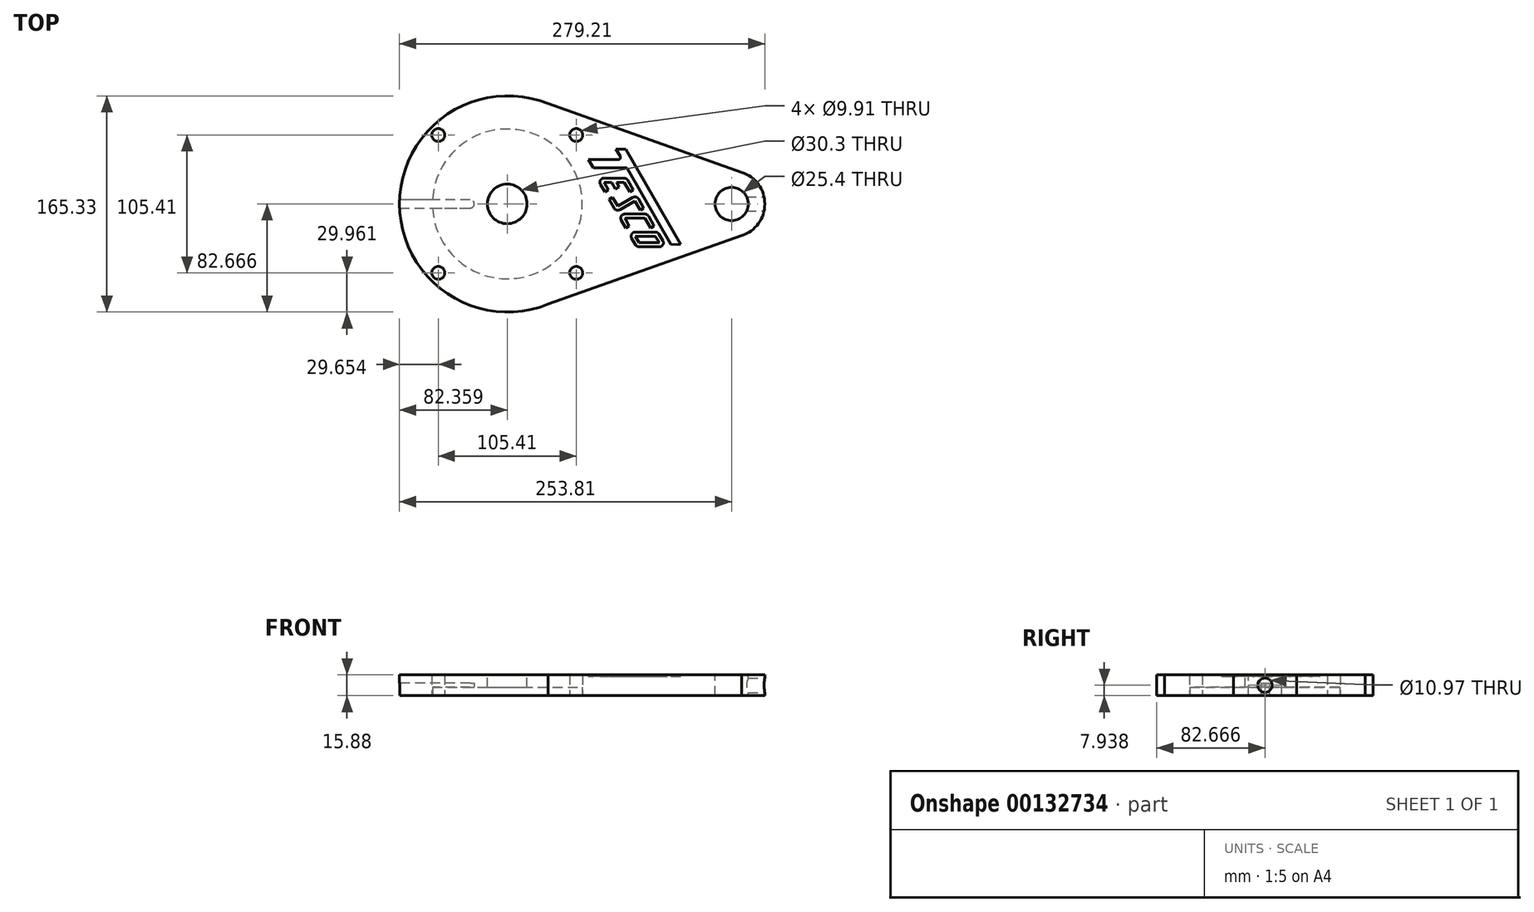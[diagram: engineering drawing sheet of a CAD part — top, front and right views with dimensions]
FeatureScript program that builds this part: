
annotation { "Feature Type Name" : "Feature", "Feature Type Description" : "" }
export const myFeature = defineFeature(function(context is Context, id is Id, definition is map)
    precondition{}
    {
        {
            var Q0;
            Q0=qCreatedBy(makeId("Top.planeOp"),FACE);
            var sketch = newSketch(context, id + "F0", { "sketchPlane" : qUnion([Q0])});
            skPoint(sketch, "E0", {"position": v(82.66, -82.66) * mm});
            skArc(sketch, "E1", {"start": v(113.6, -6) * mm, "mid": v(0, -82.66) * mm, "end": v(113.6, -159.32) * mm});
            skPoint(sketch, "E2", {"position": v(253.8, -82.66) * mm});
            skArc(sketch, "E3", {"start": v(261.56, -106.85) * mm, "mid": v(279.2, -82.66) * mm, "end": v(261.56, -58.48) * mm});
            skLineSegment(sketch, "E4", {"start": v(263.02, -59) * mm, "end": v(113.6, -6) * mm});
            skLineSegment(sketch, "E5.MirrorCS", {"start": v(263.02, -106.33) * mm, "end": v(113.6, -159.32) * mm});
            skPoint(sketch, "E6.orphan", {"position": v(279.2, -165.33) * mm});
            skPoint(sketch, "E7.orphan", {"position": v(279.2, 0) * mm});
            skPoint(sketch, "E8.orphan", {"position": v(0, 0) * mm});
            skPoint(sketch, "E9.top.start.orphan", {"position": v(0, -165.33) * mm});
            skPoint(sketch, "E10.start.orphan", {"position": v(0, -82.66) * mm});
            skPoint(sketch, "E11.trimOffspring.end.orphan", {"position": v(279.2, -82.66) * mm});
            skSolve(sketch);
        }
        {
            var Q0;
            Q0 = qSketchRegion(id + "F0", true);
            extrude(context, id + "F1", {"entities" : qUnion([Q0]), "depth" : 15.88 * mm});
        }
        {
            var Q0;
            Q0=makeQuery(id+"F1.opExtrude","CAP_FACE",FACE,{"disambiguationData":[OSD([sQuery(id+"F0.wireOp",EDGE,"E1"),sQuery(id+"F0.wireOp",EDGE,"E3"),sQuery(id+"F0.wireOp",EDGE,"E4"),sQuery(id+"F0.wireOp",EDGE,"E5.MirrorCS")])],"isStart":false});
            var sketch = newSketch(context, id + "F2", { "sketchPlane" : qUnion([Q0])});
            skLineSegment(sketch, "E12", {"start": v(0, -82.66) * mm, "end": v(279.2, -82.66) * mm});
            skPoint(sketch, "E13", {"position": v(253.8, -82.66) * mm});
            skCircle(sketch, "E14", {"center": v(253.8, -82.66) * mm, "radius": 12.7 * mm});
            skSolve(sketch);
        }
        {
            var Q0;
            Q0 = qSketchRegion(id + "F2", true);
            extrude(context, id + "F3", {"entities" : qUnion([Q0]), "operationType" : NewBodyOperationType.REMOVE, "endBound" : BoundingType.THROUGH_ALL, "oppositeDirection" : true, "depth" : 25.4 * mm});
        }
        {
            var Q0;
            Q0=makeQuery(id+"F1.opExtrude","CAP_FACE",FACE,{"disambiguationData":[OSD([sQuery(id+"F0.wireOp",EDGE,"E1"),sQuery(id+"F0.wireOp",EDGE,"E3"),sQuery(id+"F0.wireOp",EDGE,"E4"),sQuery(id+"F0.wireOp",EDGE,"E5.MirrorCS")])],"isStart":false});
            var sketch = newSketch(context, id + "F4", { "sketchPlane" : qUnion([Q0])});
            skPoint(sketch, "E15", {"position": v(82.36, -82.66) * mm});
            skPoint(sketch, "E15.positionSnap0", {"position": v(0, -82.66) * mm});
            skPoint(sketch, "E16", {"position": v(253.8, -82.66) * mm});
            skCircle(sketch, "E17", {"center": v(82.36, -82.66) * mm, "radius": 15.15 * mm});
            skSolve(sketch);
        }
        {
            var Q0;
            Q0 = qSketchRegion(id + "F4", true);
            extrude(context, id + "F5", {"entities" : qUnion([Q0]), "operationType" : NewBodyOperationType.REMOVE, "endBound" : BoundingType.THROUGH_ALL, "oppositeDirection" : true, "depth" : 25.4 * mm});
        }
        {
            var Q0;
            Q0=makeQuery(id+"F1.opExtrude","CAP_FACE",FACE,{"disambiguationData":[OSD([sQuery(id+"F0.wireOp",EDGE,"E1"),sQuery(id+"F0.wireOp",EDGE,"E3"),sQuery(id+"F0.wireOp",EDGE,"E4"),sQuery(id+"F0.wireOp",EDGE,"E5.MirrorCS")])],"isStart":true});
            var sketch = newSketch(context, id + "F6", { "sketchPlane" : qUnion([Q0])});
            skPoint(sketch, "E18", {"position": v(82.36, 82.66) * mm});
            skCircle(sketch, "E19", {"center": v(82.36, 82.66) * mm, "radius": 57.28 * mm});
            skSolve(sketch);
        }
        {
            var Q0;
            Q0 = qSketchRegion(id + "F6", true);
            extrude(context, id + "F7", {"entities" : qUnion([Q0]), "operationType" : NewBodyOperationType.REMOVE, "oppositeDirection" : true, "depth" : 6.35 * mm});
        }
        {
            var Q0;
            Q0=makeQuery(id+"F1.opExtrude","CAP_FACE",FACE,{"disambiguationData":[OSD([sQuery(id+"F0.wireOp",EDGE,"E1"),sQuery(id+"F0.wireOp",EDGE,"E3"),sQuery(id+"F0.wireOp",EDGE,"E4"),sQuery(id+"F0.wireOp",EDGE,"E5.MirrorCS")])],"isStart":true});
            var sketch = newSketch(context, id + "F8", { "sketchPlane" : qUnion([Q0])});
            skLineSegment(sketch, "E20", {"start": v(0, 82.66) * mm, "end": v(279.2, 82.66) * mm});
            skPoint(sketch, "E21", {"position": v(82.36, 82.66) * mm});
            skCircle(sketch, "E22", {"center": v(29.65, 135.37) * mm, "radius": 4.95 * mm});
            skCircle(sketch, "E23", {"center": v(135.06, 135.37) * mm, "radius": 4.95 * mm});
            skCircle(sketch, "E24", {"center": v(135.06, 29.96) * mm, "radius": 4.95 * mm});
            skCircle(sketch, "E25", {"center": v(29.65, 29.96) * mm, "radius": 4.95 * mm});
            skSolve(sketch);
        }
        {
            var Q0;
            Q0 = qSketchRegion(id + "F8", true);
            extrude(context, id + "F9", {"entities" : qUnion([Q0]), "operationType" : NewBodyOperationType.REMOVE, "endBound" : BoundingType.THROUGH_ALL, "oppositeDirection" : true, "depth" : 25.4 * mm});
        }
        {
            var Q0;
            Q0=makeQuery(id+"F1.opExtrude","CAP_FACE",FACE,{"disambiguationData":[OSD([sQuery(id+"F0.wireOp",EDGE,"E1"),sQuery(id+"F0.wireOp",EDGE,"E3"),sQuery(id+"F0.wireOp",EDGE,"E4"),sQuery(id+"F0.wireOp",EDGE,"E5.MirrorCS")])],"isStart":true});
            var sketch = newSketch(context, id + "F10", { "sketchPlane" : qUnion([Q0])});
            skPoint(sketch, "E26", {"position": v(57.15, 82.66) * mm});
            skPoint(sketch, "E27.orphan", {"position": v(82.36, 82.66) * mm});
            skLineSegment(sketch, "E28", {"start": v(53.98, 85.84) * mm, "end": v(0.06, 85.84) * mm});
            skLineSegment(sketch, "E29.MirrorCS", {"start": v(53.98, 79.49) * mm, "end": v(-1.51, 79.49) * mm});
            skLineSegment(sketch, "E30", {"start": v(57.15, 82.66) * mm, "end": v(57.15, 82.66) * mm});
            skLineSegment(sketch, "E31", {"start": v(-2.49, 85.84) * mm, "end": v(-2.49, 79.49) * mm});
            skLineSegment(sketch, "E32", {"start": v(-2.49, 79.49) * mm, "end": v(-1.51, 79.49) * mm});
            skLineSegment(sketch, "E33", {"start": v(-2.49, 85.84) * mm, "end": v(0.06, 85.84) * mm});
            skPoint(sketch, "E34.visualSharp", {"position": v(57.15, 85.84) * mm});
            skArc(sketch, "E34.filletArc", {"start": v(57.15, 82.66) * mm, "mid": v(56.22, 84.9) * mm, "end": v(53.98, 85.84) * mm});
            skPoint(sketch, "E35.visualSharp", {"position": v(57.15, 79.49) * mm});
            skArc(sketch, "E35.filletArc", {"start": v(53.98, 79.49) * mm, "mid": v(56.22, 80.42) * mm, "end": v(57.15, 82.66) * mm});
            skSolve(sketch);
        }
        {
            var Q0;
            Q0 = qSketchRegion(id + "F10", true);
            extrude(context, id + "F11", {"entities" : qUnion([Q0]), "operationType" : NewBodyOperationType.REMOVE, "oppositeDirection" : true, "depth" : 9.52 * mm});
        }
        {
            var Q0;
            Q0=qCreatedBy(makeId("Right.planeOp"),FACE);
            cPlane(context, id + "F12", {"entities" : qUnion([Q0]), "cplaneType" : CPlaneType.OFFSET, "offset" : 279.4 * mm, "width" : 152.4 * mm, "height" : 152.4 * mm});
        }
        {
            var Q0;
            Q0=qCreatedBy(id+"F12.planeOp",FACE);
            var sketch = newSketch(context, id + "F13", { "sketchPlane" : qUnion([Q0])});
            skPoint(sketch, "E36", {"position": v(-82.66, 0) * mm});
            skPoint(sketch, "E37", {"position": v(-82.66, 7.94) * mm});
            skCircle(sketch, "E38", {"center": v(-82.66, 7.94) * mm, "radius": 5.49 * mm});
            skSolve(sketch);
        }
        {
            var Q0;
            Q0 = qSketchRegion(id + "F13", true);
            extrude(context, id + "F14", {"entities" : qUnion([Q0]), "operationType" : NewBodyOperationType.REMOVE, "oppositeDirection" : true, "depth" : 15.88 * mm});
        }
        {
            var Q0;
            Q0=makeQuery(id+"F1.opExtrude","CAP_FACE",FACE,{"disambiguationData":[OSD([sQuery(id+"F0.wireOp",EDGE,"E1"),sQuery(id+"F0.wireOp",EDGE,"E3"),sQuery(id+"F0.wireOp",EDGE,"E4"),sQuery(id+"F0.wireOp",EDGE,"E5.MirrorCS")])],"isStart":false});
            var sketch = newSketch(context, id + "F15", { "sketchPlane" : qUnion([Q0])});
            skLineSegment(sketch, "E39", {"start": v(144.39, -48.66) * mm, "end": v(148.05, -55.01) * mm});
            skLineSegment(sketch, "E40", {"start": v(165.47, -40.73) * mm, "end": v(168.67, -46.28) * mm});
            skLineSegment(sketch, "E41.0", {"start": v(172.9, -40.9) * mm, "end": v(214.81, -113.5) * mm});
            skLineSegment(sketch, "E42.0", {"start": v(167.3, -48.66) * mm, "end": v(144.39, -48.66) * mm});
            skLineSegment(sketch, "E43.0", {"start": v(172.8, -55.01) * mm, "end": v(148.05, -55.01) * mm});
            skLineSegment(sketch, "E44", {"start": v(172.9, -40.9) * mm, "end": v(165.47, -40.73) * mm});
            skPoint(sketch, "E45.orphan", {"position": v(139.8, -40.73) * mm});
            skLineSegment(sketch, "E46", {"start": v(214.81, -113.5) * mm, "end": v(207.67, -113.83) * mm});
            skLineSegment(sketch, "E47.trimOffspring", {"start": v(174.17, -55.8) * mm, "end": v(207.67, -113.83) * mm});
            skLineSegment(sketch, "E48", {"start": v(158.3, -72.77) * mm, "end": v(158.31, -72.78) * mm});
            skLineSegment(sketch, "E49", {"start": v(177.36, -72.77) * mm, "end": v(177.36, -72.78) * mm});
            skPoint(sketch, "E50.visualSharp", {"position": v(170.05, -48.66) * mm});
            skArc(sketch, "E50.filletArc", {"start": v(167.3, -48.66) * mm, "mid": v(168.67, -47.87) * mm, "end": v(168.67, -46.28) * mm});
            skPoint(sketch, "E51.visualSharp", {"position": v(173.72, -55.01) * mm});
            skArc(sketch, "E51.filletArc", {"start": v(174.17, -55.8) * mm, "mid": v(173.6, -55.22) * mm, "end": v(172.8, -55.01) * mm});
            skPoint(sketch, "E52.visualSharp", {"position": v(172.6, -64.54) * mm});
            skPoint(sketch, "E53.visualSharp", {"position": v(153.55, -64.54) * mm});
            skPoint(sketch, "E54.visualSharp", {"position": v(166.25, -86.53) * mm});
            skPoint(sketch, "E55.visualSharp", {"position": v(180.54, -78.28) * mm});
            skPoint(sketch, "E56.visualSharp", {"position": v(188.48, -92.03) * mm});
            skPoint(sketch, "E57.visualSharp", {"position": v(169.43, -92.03) * mm});
            skPoint(sketch, "E58.visualSharp", {"position": v(177.36, -105.78) * mm});
            skPoint(sketch, "E59.visualSharp", {"position": v(182.31, -113.92) * mm});
            skPoint(sketch, "E60.visualSharp", {"position": v(201.36, -113.92) * mm});
            skPoint(sketch, "E61.visualSharp", {"position": v(196.41, -105.78) * mm});
            skLineSegment(sketch, "E62.0", {"start": v(171.68, -66.12) * mm, "end": v(175.98, -73.56) * mm});
            skLineSegment(sketch, "E62.1", {"start": v(156.3, -66.12) * mm, "end": v(159.68, -71.98) * mm});
            skLineSegment(sketch, "E62.2", {"start": v(156.3, -66.12) * mm, "end": v(156.3, -66.12) * mm});
            skLineSegment(sketch, "E62.3", {"start": v(171.68, -66.12) * mm, "end": v(165.83, -66.12) * mm});
            skLineSegment(sketch, "E62.4", {"start": v(171.68, -66.12) * mm, "end": v(171.68, -66.12) * mm});
            skLineSegment(sketch, "E63.0", {"start": v(174.43, -64.54) * mm, "end": v(178.73, -71.98) * mm});
            skLineSegment(sketch, "E63.1", {"start": v(153.55, -67.71) * mm, "end": v(156.93, -73.56) * mm});
            skArc(sketch, "E63.2", {"start": v(156.3, -62.95) * mm, "mid": v(153.55, -64.54) * mm, "end": v(153.55, -67.71) * mm});
            skLineSegment(sketch, "E63.3", {"start": v(171.68, -62.95) * mm, "end": v(156.3, -62.95) * mm});
            skArc(sketch, "E63.4", {"start": v(174.43, -64.54) * mm, "mid": v(173.27, -63.37) * mm, "end": v(171.68, -62.95) * mm});
            skLineSegment(sketch, "E64", {"start": v(178.73, -71.98) * mm, "end": v(175.98, -73.56) * mm});
            skLineSegment(sketch, "E65", {"start": v(159.68, -71.98) * mm, "end": v(156.93, -73.56) * mm});
            skPoint(sketch, "E66.orphan", {"position": v(163.08, -64.54) * mm});
            skLineSegment(sketch, "E67.0", {"start": v(162.15, -66.11) * mm, "end": v(165.1, -71.2) * mm});
            skLineSegment(sketch, "E68.0", {"start": v(165.81, -66.1) * mm, "end": v(167.84, -69.62) * mm});
            skLineSegment(sketch, "E69", {"start": v(167.84, -69.62) * mm, "end": v(165.1, -71.2) * mm});
            skLineSegment(sketch, "E70.trimOffspring", {"start": v(162.16, -66.12) * mm, "end": v(156.3, -66.12) * mm});
            skLineSegment(sketch, "E71.0", {"start": v(162.86, -77.49) * mm, "end": v(166.83, -84.36) * mm});
            skLineSegment(sketch, "E71.1", {"start": v(186.68, -85.74) * mm, "end": v(182.7, -78.86) * mm});
            skArc(sketch, "E71.2", {"start": v(182.7, -78.86) * mm, "mid": v(180.78, -77.39) * mm, "end": v(178.37, -77.7) * mm});
            skLineSegment(sketch, "E71.3", {"start": v(178.37, -77.7) * mm, "end": v(166.83, -84.36) * mm});
            skLineSegment(sketch, "E71.4", {"start": v(166.83, -84.36) * mm, "end": v(166.83, -84.36) * mm});
            skLineSegment(sketch, "E72.0", {"start": v(160.11, -79.08) * mm, "end": v(164.08, -85.95) * mm});
            skArc(sketch, "E72.1", {"start": v(164.08, -85.95) * mm, "mid": v(166.01, -87.43) * mm, "end": v(168.42, -87.11) * mm});
            skLineSegment(sketch, "E72.2", {"start": v(179.96, -80.45) * mm, "end": v(168.42, -87.11) * mm});
            skLineSegment(sketch, "E72.3", {"start": v(183.93, -87.33) * mm, "end": v(179.96, -80.45) * mm});
            skLineSegment(sketch, "E73", {"start": v(186.68, -85.74) * mm, "end": v(183.93, -87.33) * mm});
            skLineSegment(sketch, "E74", {"start": v(162.86, -77.49) * mm, "end": v(160.11, -79.08) * mm});
            skLineSegment(sketch, "E75.0", {"start": v(187.56, -93.62) * mm, "end": v(191.86, -101.07) * mm});
            skLineSegment(sketch, "E75.1", {"start": v(172.18, -93.62) * mm, "end": v(175.56, -99.49) * mm});
            skLineSegment(sketch, "E75.2", {"start": v(172.18, -93.62) * mm, "end": v(172.18, -93.62) * mm});
            skLineSegment(sketch, "E75.3", {"start": v(172.18, -93.62) * mm, "end": v(187.56, -93.62) * mm});
            skLineSegment(sketch, "E75.4", {"start": v(187.56, -93.62) * mm, "end": v(187.56, -93.62) * mm});
            skLineSegment(sketch, "E76.0", {"start": v(190.3, -92.03) * mm, "end": v(194.61, -99.49) * mm});
            skLineSegment(sketch, "E76.1", {"start": v(169.43, -95.2) * mm, "end": v(172.81, -101.07) * mm});
            skArc(sketch, "E76.2", {"start": v(172.18, -90.44) * mm, "mid": v(169.43, -92.03) * mm, "end": v(169.43, -95.2) * mm});
            skLineSegment(sketch, "E76.3", {"start": v(172.18, -90.44) * mm, "end": v(187.56, -90.44) * mm});
            skArc(sketch, "E76.4", {"start": v(190.3, -92.03) * mm, "mid": v(189.15, -90.87) * mm, "end": v(187.56, -90.44) * mm});
            skLineSegment(sketch, "E77", {"start": v(194.61, -99.49) * mm, "end": v(191.86, -101.07) * mm});
            skLineSegment(sketch, "E78", {"start": v(175.56, -99.49) * mm, "end": v(172.81, -101.07) * mm});
            skLineSegment(sketch, "E79.0", {"start": v(195.52, -107.37) * mm, "end": v(195.52, -107.37) * mm});
            skLineSegment(sketch, "E79.1", {"start": v(180.19, -107.37) * mm, "end": v(195.52, -107.37) * mm});
            skLineSegment(sketch, "E79.2", {"start": v(195.52, -107.37) * mm, "end": v(198.54, -112.33) * mm});
            skLineSegment(sketch, "E79.3", {"start": v(180.19, -107.37) * mm, "end": v(180.19, -107.37) * mm});
            skLineSegment(sketch, "E79.4", {"start": v(198.54, -112.33) * mm, "end": v(198.54, -112.33) * mm});
            skLineSegment(sketch, "E79.5", {"start": v(198.54, -112.33) * mm, "end": v(183.2, -112.33) * mm});
            skLineSegment(sketch, "E79.6", {"start": v(183.2, -112.33) * mm, "end": v(183.2, -112.33) * mm});
            skLineSegment(sketch, "E79.7", {"start": v(183.2, -112.33) * mm, "end": v(180.19, -107.37) * mm});
            skLineSegment(sketch, "E80.0", {"start": v(198.23, -105.72) * mm, "end": v(201.25, -110.68) * mm});
            skArc(sketch, "E80.1", {"start": v(198.54, -115.5) * mm, "mid": v(201.3, -113.89) * mm, "end": v(201.25, -110.68) * mm});
            skArc(sketch, "E80.2", {"start": v(198.23, -105.72) * mm, "mid": v(197.08, -104.6) * mm, "end": v(195.52, -104.2) * mm});
            skLineSegment(sketch, "E80.3", {"start": v(198.54, -115.5) * mm, "end": v(183.2, -115.5) * mm});
            skLineSegment(sketch, "E80.4", {"start": v(180.19, -104.2) * mm, "end": v(195.52, -104.2) * mm});
            skArc(sketch, "E80.5", {"start": v(180.19, -104.2) * mm, "mid": v(177.42, -105.81) * mm, "end": v(177.47, -109.02) * mm});
            skLineSegment(sketch, "E80.6", {"start": v(180.5, -113.98) * mm, "end": v(177.47, -109.02) * mm});
            skArc(sketch, "E80.7", {"start": v(180.5, -113.98) * mm, "mid": v(181.65, -115.1) * mm, "end": v(183.2, -115.5) * mm});
            skSolve(sketch);
        }
        {
            var Q0;
            Q0 = qSketchRegion(id + "F15", true);
            extrude(context, id + "F16", {"entities" : qUnion([Q0]), "operationType" : NewBodyOperationType.REMOVE, "oppositeDirection" : true, "depth" : 1.27 * mm});
        }
    });
